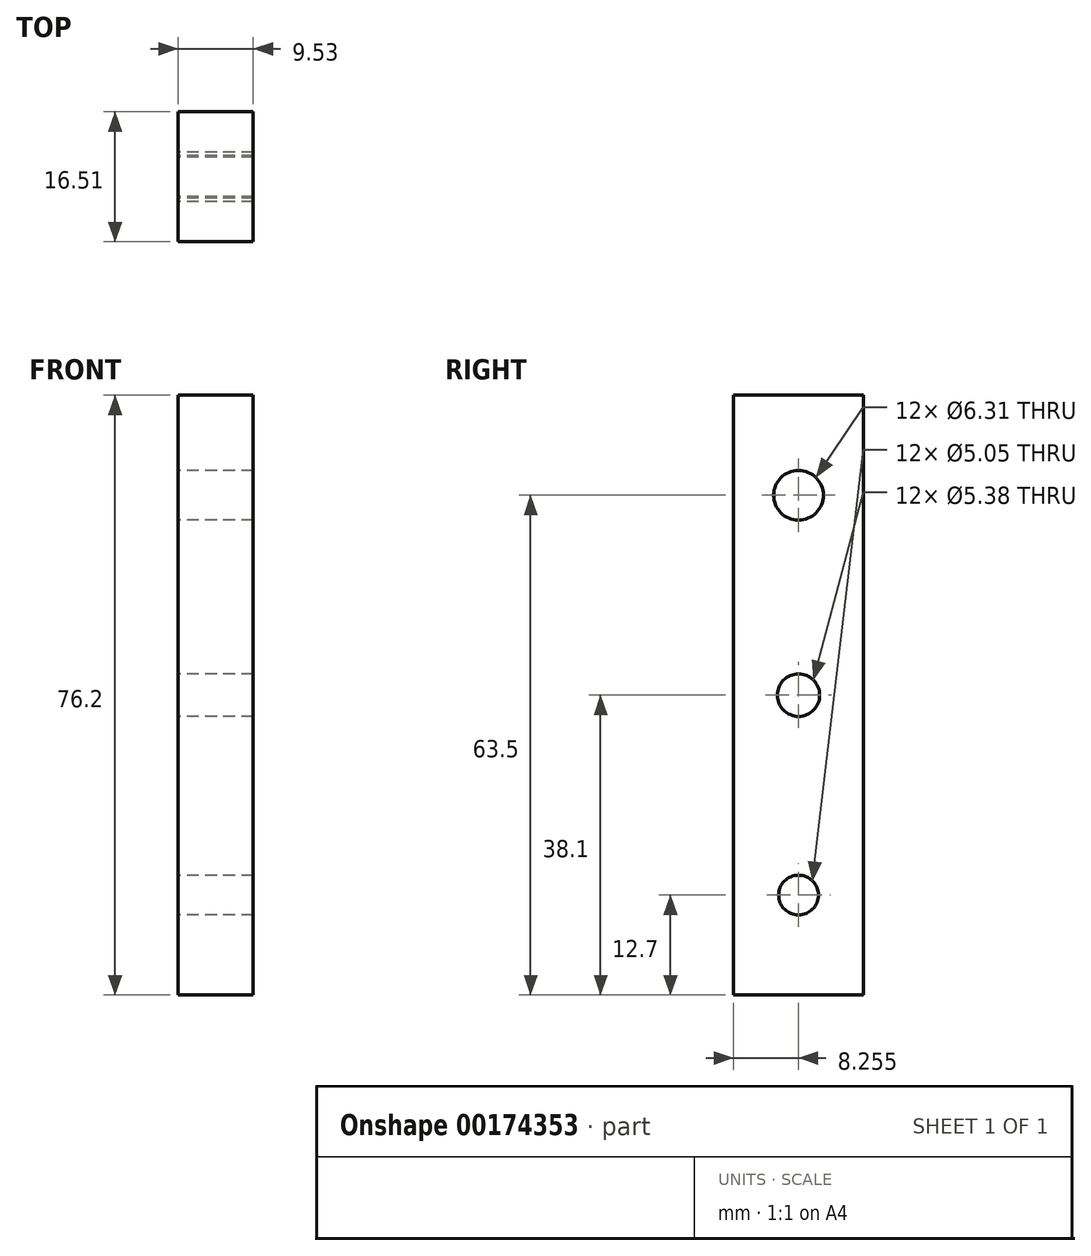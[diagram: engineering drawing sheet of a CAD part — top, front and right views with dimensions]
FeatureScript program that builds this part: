
annotation { "Feature Type Name" : "Feature", "Feature Type Description" : "" }
export const myFeature = defineFeature(function(context is Context, id is Id, definition is map)
    precondition{}
    {
        {
            var Q0;
            Q0=qCreatedBy(makeId("Right.planeOp"),FACE);
            var sketch = newSketch(context, id + "F0", { "sketchPlane" : qUnion([Q0])});
            skLineSegment(sketch, "E0.bottom", {"start": v(0, 0) * mm, "end": v(-16.51, 0) * mm});
            skLineSegment(sketch, "E0.top", {"start": v(0, 76.2) * mm, "end": v(-16.51, 76.2) * mm});
            skLineSegment(sketch, "E0.left", {"start": v(0, 0) * mm, "end": v(0, 76.2) * mm});
            skLineSegment(sketch, "E0.right", {"start": v(-16.51, 0) * mm, "end": v(-16.51, 76.2) * mm});
            skCircle(sketch, "E1", {"center": v(-8.26, 63.5) * mm, "radius": 3.16 * mm});
            skCircle(sketch, "E2", {"center": v(-8.25, 12.7) * mm, "radius": 2.52 * mm});
            skCircle(sketch, "E3", {"center": v(-8.26, 38.1) * mm, "radius": 2.7 * mm});
            skSolve(sketch);
        }
        {
            var Q0;
            Q0=makeQuery(id+"F0.imprint","IMPRINT",FACE,{"disambiguationData":[TD([[makeQuery(id+"F0.imprint","IMPRINT",EDGE,{"derivedFrom":sQuery(id+"F0.wireOp",EDGE,"E0.bottom")}),-1.0]])]});
            extrude(context, id + "F1", {"entities" : qUnion([Q0]), "depth" : 9.52 * mm});
        }
    });
